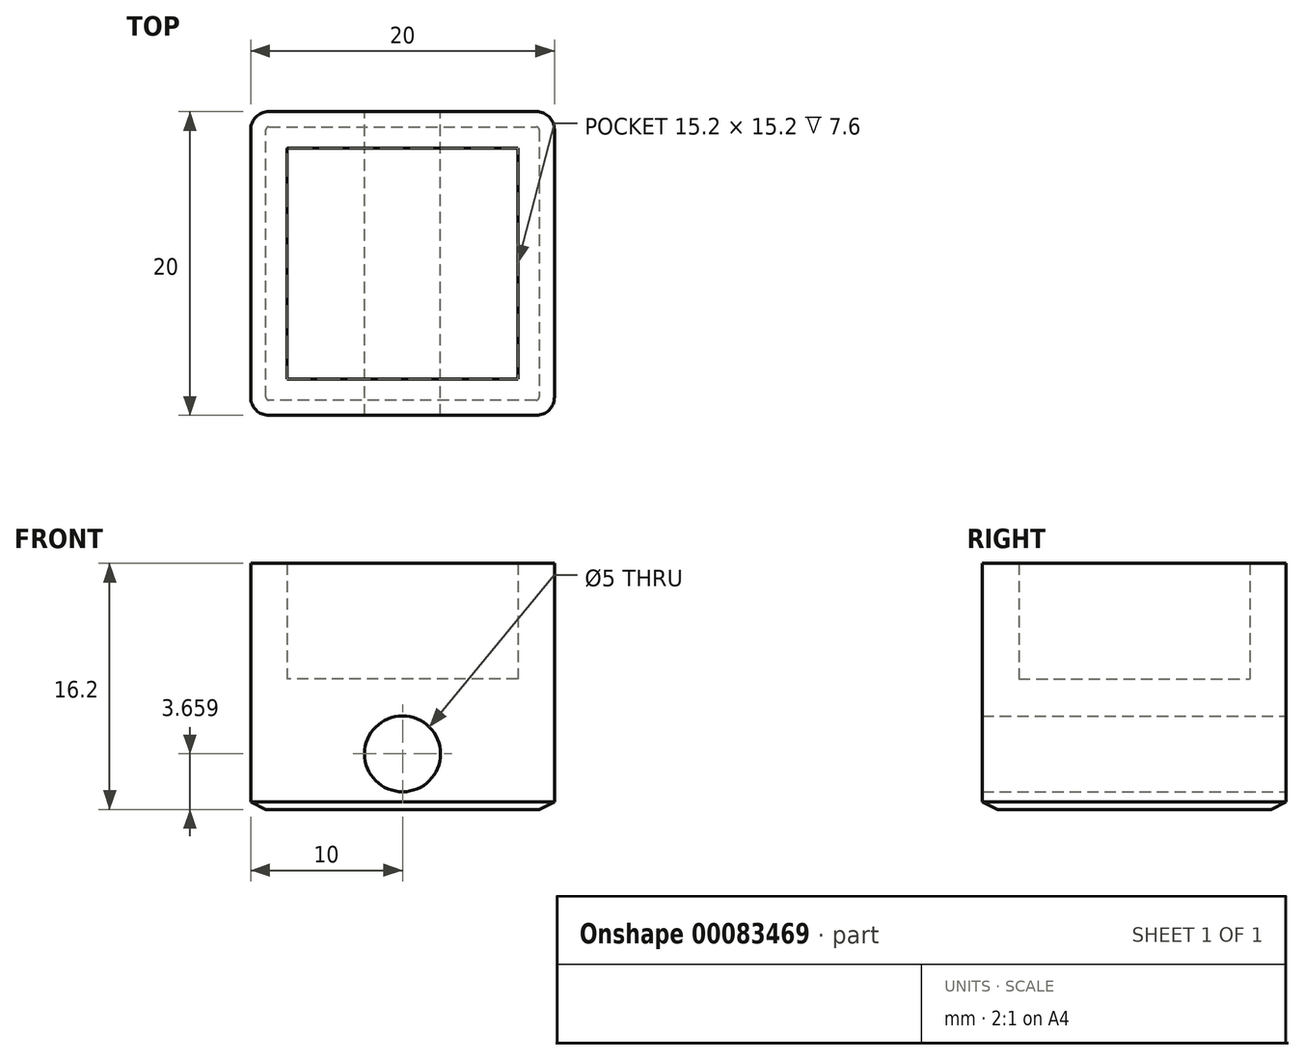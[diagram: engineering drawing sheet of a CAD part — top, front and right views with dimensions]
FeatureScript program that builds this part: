
annotation { "Feature Type Name" : "Feature", "Feature Type Description" : "" }
export const myFeature = defineFeature(function(context is Context, id is Id, definition is map)
    precondition{}
    {
        {
            var Q0;
            Q0=qCreatedBy(makeId("Top.planeOp"),FACE);
            var sketch = newSketch(context, id + "F0", { "sketchPlane" : qUnion([Q0])});
            skLineSegment(sketch, "E0.bottom", {"start": v(7.6, -7.6) * mm, "end": v(-7.6, -7.6) * mm});
            skLineSegment(sketch, "E0.top", {"start": v(7.6, 7.6) * mm, "end": v(-7.6, 7.6) * mm});
            skLineSegment(sketch, "E0.left", {"start": v(7.6, -7.6) * mm, "end": v(7.6, 7.6) * mm});
            skLineSegment(sketch, "E0.right", {"start": v(-7.6, -7.6) * mm, "end": v(-7.6, 7.6) * mm});
            skPoint(sketch, "E0.middle", {"position": v(0, 0) * mm});
            skLineSegment(sketch, "E1.0", {"start": v(10, 10) * mm, "end": v(-10, 10) * mm});
            skLineSegment(sketch, "E1.1", {"start": v(10, -10) * mm, "end": v(10, 10) * mm});
            skLineSegment(sketch, "E1.2", {"start": v(10, -10) * mm, "end": v(-10, -10) * mm});
            skLineSegment(sketch, "E1.3", {"start": v(-10, -10) * mm, "end": v(-10, 10) * mm});
            skSolve(sketch);
        }
        {
            var Q0;
            Q0=makeQuery(id+"F0.imprint","IMPRINT",FACE,{"disambiguationData":[TD([[makeQuery(id+"F0.imprint","IMPRINT",EDGE,{"derivedFrom":sQuery(id+"F0.wireOp",EDGE,"E0.bottom")}),1.0]])]});
            var Q1;
            Q1=makeQuery(id+"F0.imprint","IMPRINT",FACE,{"disambiguationData":[TD([[makeQuery(id+"F0.imprint","IMPRINT",EDGE,{"derivedFrom":sQuery(id+"F0.wireOp",EDGE,"E0.bottom")}),-1.0]])]});
            extrude(context, id + "F1", {"entities" : qUnion([Q0, Q1]), "depth" : 10 * mm, "offsetDistance" : 25 * mm});
        }
        {
            var Q0;
            Q0=makeQuery(id+"F1.opExtrude","CAP_FACE",FACE,{"disambiguationData":[OSD([sQuery(id+"F0.wireOp",EDGE,"E1.0"),sQuery(id+"F0.wireOp",EDGE,"E1.1"),sQuery(id+"F0.wireOp",EDGE,"E1.2"),sQuery(id+"F0.wireOp",EDGE,"E1.3")])],"isStart":false});
            shell(context, id + "F2", {"entities" : qUnion([Q0]), "thickness" : 2.4 * mm});
        }
        {
            var Q0;
            Q0=makeQuery(id+"F1.opExtrude","CAP_FACE",FACE,{"disambiguationData":[OSD([sQuery(id+"F0.wireOp",EDGE,"E1.0"),sQuery(id+"F0.wireOp",EDGE,"E1.1"),sQuery(id+"F0.wireOp",EDGE,"E1.2"),sQuery(id+"F0.wireOp",EDGE,"E1.3")])],"isStart":true});
            extrude(context, id + "F3", {"entities" : qUnion([Q0]), "operationType" : NewBodyOperationType.ADD, "depth" : 6.2 * mm, "offsetDistance" : 25 * mm});
        }
        {
            var Q0;
            {var subQ0=sQuery(id+"F0.wireOp",EDGE,"E1.0");Q0=makeQuery(id+"F3.boolean.opBoolean","MERGE",FACE,{"derivedFrom":[makeQuery(id+"F1.opExtrude","SWEPT_FACE",FACE,{"disambiguationData":[OSD([subQ0])]}),makeQuery(id+"F3.opExtrude","SWEPT_FACE",FACE,{"disambiguationData":[OSD([subQ0])]})]});}
            var sketch = newSketch(context, id + "F4", { "sketchPlane" : qUnion([Q0])});
            skCircle(sketch, "E2", {"center": v(0, -2.54) * mm, "radius": 2.5 * mm});
            skSolve(sketch);
        }
        {
            var Q0;
            Q0=makeQuery(id+"F4.imprint","IMPRINT",FACE,{"disambiguationData":[TD([[makeQuery(id+"F4.imprint","IMPRINT",EDGE,{"derivedFrom":sQuery(id+"F4.wireOp",EDGE,"E2")}),1.0]])]});
            extrude(context, id + "F5", {"entities" : qUnion([Q0]), "operationType" : NewBodyOperationType.REMOVE, "endBound" : BoundingType.THROUGH_ALL, "oppositeDirection" : true, "depth" : 25 * mm, "offsetDistance" : 25 * mm});
        }
        {
            var Q0;
            {var subQ0=sQuery(id+"F0.wireOp",EDGE,"E1.3");var subQ1=sQuery(id+"F0.wireOp",EDGE,"E1.0");Q0=makeQuery(id+"F3.boolean.opBoolean","MERGE",EDGE,{"derivedFrom":[makeQuery(id+"F1.opExtrude","SWEPT_EDGE",EDGE,{"disambiguationData":[OSD([subQ1,subQ0])]}),makeQuery(id+"F3.opExtrude","SWEPT_EDGE",EDGE,{"disambiguationData":[OSD([subQ1,subQ0])]})]});}
            var Q1;
            {var subQ0=sQuery(id+"F0.wireOp",EDGE,"E1.1");var subQ1=sQuery(id+"F0.wireOp",EDGE,"E1.0");Q1=makeQuery(id+"F3.boolean.opBoolean","MERGE",EDGE,{"derivedFrom":[makeQuery(id+"F1.opExtrude","SWEPT_EDGE",EDGE,{"disambiguationData":[OSD([subQ1,subQ0])]}),makeQuery(id+"F3.opExtrude","SWEPT_EDGE",EDGE,{"disambiguationData":[OSD([subQ1,subQ0])]})]});}
            var Q2;
            {var subQ0=sQuery(id+"F0.wireOp",EDGE,"E1.2");var subQ1=sQuery(id+"F0.wireOp",EDGE,"E1.1");Q2=makeQuery(id+"F3.boolean.opBoolean","MERGE",EDGE,{"derivedFrom":[makeQuery(id+"F1.opExtrude","SWEPT_EDGE",EDGE,{"disambiguationData":[OSD([subQ1,subQ0])]}),makeQuery(id+"F3.opExtrude","SWEPT_EDGE",EDGE,{"disambiguationData":[OSD([subQ1,subQ0])]})]});}
            var Q3;
            {var subQ0=sQuery(id+"F0.wireOp",EDGE,"E1.3");var subQ1=sQuery(id+"F0.wireOp",EDGE,"E1.2");Q3=makeQuery(id+"F3.boolean.opBoolean","MERGE",EDGE,{"derivedFrom":[makeQuery(id+"F1.opExtrude","SWEPT_EDGE",EDGE,{"disambiguationData":[OSD([subQ1,subQ0])]}),makeQuery(id+"F3.opExtrude","SWEPT_EDGE",EDGE,{"disambiguationData":[OSD([subQ1,subQ0])]})]});}
            fillet(context, id + "F6", {"entities" : qUnion([Q0, Q1, Q2, Q3]), "radius" : 1.2 * mm, "tangentPropagation" : true, "allowEdgeOverflow" : false});
        }
        {
            var Q0;
            Q0=makeQuery(id+"F3.opExtrude","CAP_FACE",FACE,{"disambiguationData":[OSD([sQuery(id+"F0.wireOp",EDGE,"E1.0"),sQuery(id+"F0.wireOp",EDGE,"E1.1"),sQuery(id+"F0.wireOp",EDGE,"E1.2"),sQuery(id+"F0.wireOp",EDGE,"E1.3")])],"isStart":false});
            chamfer(context, id + "F7", {"entities" : qUnion([Q0]), "chamferType" : ChamferType.TWO_OFFSETS, "width1" : 1 * mm, "oppositeDirection" : false, "width2" : .5 * mm, "tangentPropagation" : true});
        }
    });
